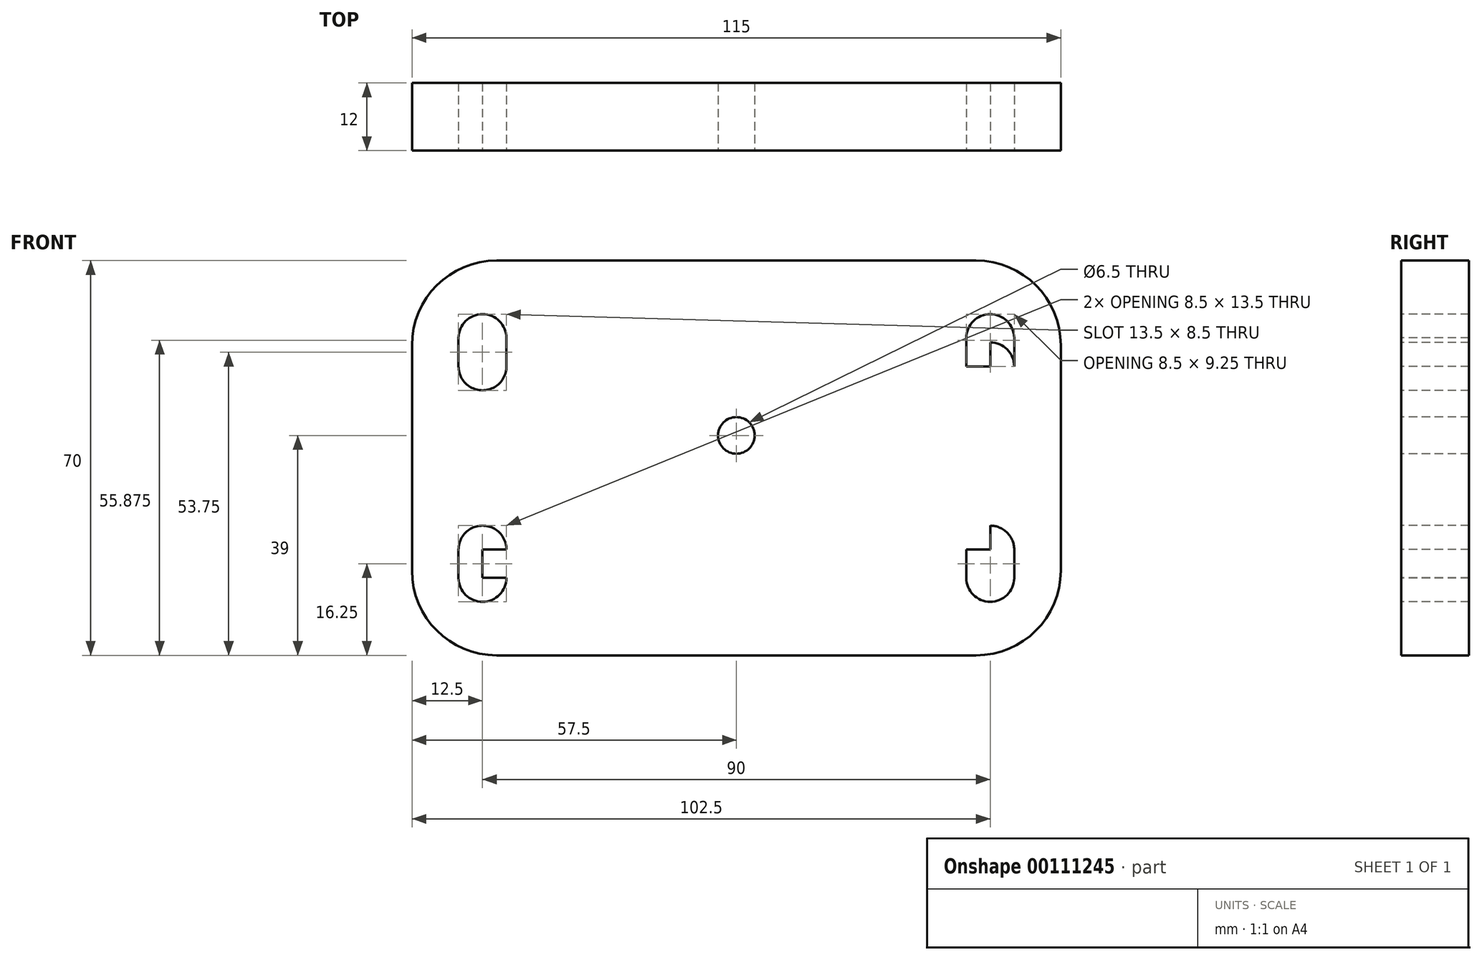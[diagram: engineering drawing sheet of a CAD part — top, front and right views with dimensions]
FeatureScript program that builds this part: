
annotation { "Feature Type Name" : "Feature", "Feature Type Description" : "" }
export const myFeature = defineFeature(function(context is Context, id is Id, definition is map)
    precondition{}
    {
        {
            var Q0;
            Q0=qCreatedBy(makeId("Front.planeOp"),FACE);
            var sketch = newSketch(context, id + "F0", { "sketchPlane" : qUnion([Q0])});
            skLineSegment(sketch, "E0.bottom", {"start": v(-57.5, 35) * mm, "end": v(57.5, 35) * mm});
            skLineSegment(sketch, "E0.top", {"start": v(-57.5, -35) * mm, "end": v(57.5, -35) * mm});
            skLineSegment(sketch, "E0.left", {"start": v(-57.5, 35) * mm, "end": v(-57.5, -35) * mm});
            skLineSegment(sketch, "E0.right", {"start": v(57.5, 35) * mm, "end": v(57.5, -35) * mm});
            skPoint(sketch, "E0.middle", {"position": v(0, 0) * mm});
            skSolve(sketch);
        }
        {
            var Q0;
            Q0 = qSketchRegion(id + "F0", true);
            extrude(context, id + "F1", {"entities" : qUnion([Q0]), "depth" : 12 * mm});
        }
        {
            var Q0;
            Q0=makeQuery(id+"F1.opExtrude","CAP_FACE",FACE,{"disambiguationData":[OSD([sQuery(id+"F0.wireOp",EDGE,"E0.bottom"),sQuery(id+"F0.wireOp",EDGE,"E0.top"),sQuery(id+"F0.wireOp",EDGE,"E0.left"),sQuery(id+"F0.wireOp",EDGE,"E0.right")])],"isStart":false});
            var sketch = newSketch(context, id + "F2", { "sketchPlane" : qUnion([Q0])});
            skLineSegment(sketch, "E1.bottom", {"start": v(-45, 21.25) * mm, "end": v(40.75, 21.25) * mm});
            skLineSegment(sketch, "E1.top", {"start": v(-45, -21.25) * mm, "end": v(45, -21.25) * mm});
            skLineSegment(sketch, "E1.left", {"start": v(-45, 16.25) * mm, "end": v(-45, -21.25) * mm});
            skLineSegment(sketch, "E1.right", {"start": v(45, 21.25) * mm, "end": v(45, -21.25) * mm});
            skPoint(sketch, "E1.middle", {"position": v(0, 0) * mm});
            skArc(sketch, "E2", {"start": v(-49.25, -21.2) * mm, "mid": v(-45.02, -25.5) * mm, "end": v(-40.75, -21.25) * mm});
            skArc(sketch, "E3.MirrorC", {"start": v(40.75, 21.25) * mm, "mid": v(45.02, 25.5) * mm, "end": v(49.25, 21.2) * mm});
            skLineSegment(sketch, "E4.bottom", {"start": v(-45, 16.25) * mm, "end": v(45, 16.25) * mm});
            skLineSegment(sketch, "E4.top", {"start": v(-45, -16.25) * mm, "end": v(45, -16.25) * mm});
            skLineSegment(sketch, "E4.left", {"start": v(-45, 16.25) * mm, "end": v(-45, -16.25) * mm});
            skLineSegment(sketch, "E4.right", {"start": v(45, 16.25) * mm, "end": v(45, -16.25) * mm});
            skArc(sketch, "E5", {"start": v(-49.25, 16.25) * mm, "mid": v(-45, 12) * mm, "end": v(-40.75, 16.25) * mm});
            skArc(sketch, "E6.MirrorC", {"start": v(49.25, 16.25) * mm, "mid": v(45, 12) * mm, "end": v(40.75, 16.25) * mm});
            skCircle(sketch, "E7.MirrorC", {"center": v(45, 16.25) * mm, "radius": 4.25 * mm});
            skArc(sketch, "E8.MirrorC", {"start": v(48.44, 18.75) * mm, "mid": v(46.31, 12.2) * mm, "end": v(40.75, 16.25) * mm});
            skArc(sketch, "E9.MirrorC", {"start": v(-49.25, -16.25) * mm, "mid": v(-45, -12) * mm, "end": v(-40.75, -16.25) * mm});
            skLineSegment(sketch, "E10", {"start": v(-49.25, 21.3) * mm, "end": v(-49.25, 16.25) * mm});
            skLineSegment(sketch, "E11", {"start": v(-40.75, 21.25) * mm, "end": v(-40.75, 16.25) * mm});
            skArc(sketch, "E12.trimOffspring", {"start": v(-40.75, 21.25) * mm, "mid": v(-45.02, 25.5) * mm, "end": v(-49.25, 21.2) * mm});
            skLineSegment(sketch, "E13.MirrorCS", {"start": v(40.75, 21.25) * mm, "end": v(40.75, 16.25) * mm});
            skLineSegment(sketch, "E14.MirrorCS", {"start": v(49.25, 21.3) * mm, "end": v(49.25, 16.25) * mm});
            skLineSegment(sketch, "E15.MirrorCS", {"start": v(-40.75, -21.25) * mm, "end": v(-40.75, -16.25) * mm});
            skLineSegment(sketch, "E16.MirrorCS", {"start": v(-49.25, -21.3) * mm, "end": v(-49.25, -16.25) * mm});
            skLineSegment(sketch, "E17.MirrorCS", {"start": v(40.75, -21.25) * mm, "end": v(40.75, -16.25) * mm});
            skLineSegment(sketch, "E18.MirrorCS", {"start": v(49.25, -21.3) * mm, "end": v(49.25, -16.25) * mm});
            skArc(sketch, "E19.trimOffspring", {"start": v(49.25, -16.25) * mm, "mid": v(45, -12) * mm, "end": v(40.75, -16.25) * mm});
            skArc(sketch, "E20.trimOffspring", {"start": v(49.25, -21.2) * mm, "mid": v(45.02, -25.5) * mm, "end": v(40.75, -21.25) * mm});
            skSolve(sketch);
        }
        {
            var Q0;
            {var subQ0=sQuery(id+"F2.wireOp",EDGE,"E4.left");var subQ1=sQuery(id+"F2.wireOp",EDGE,"E4.bottom");var subQ2=makeQuery(id+"F2.imprint","INTERSECT",VERTEX,{"derivedFrom":[subQ1,subQ0]});Q0=makeQuery(id+"F2.imprint","IMPRINT",FACE,{"disambiguationData":[TD([[makeQuery(id+"F2.imprint","IMPRINT",EDGE,{"disambiguationData":[TD([[subQ2,-1.0]])],"derivedFrom":subQ0}),1.0]])]});}
            var Q1;
            {var subQ10=sQuery(id+"F2.wireOp",EDGE,"E11");Q1=makeQuery(id+"F2.imprint","IMPRINT",FACE,{"disambiguationData":[TD([[makeQuery(id+"F2.imprint","IMPRINT",EDGE,{"derivedFrom":subQ10}),-1.0]])]});}
            var Q2;
            {var subQ0=sQuery(id+"F2.wireOp",EDGE,"E4.left");var subQ3=sQuery(id+"F2.wireOp",EDGE,"E9.MirrorC");var subQ5=makeQuery(id+"F2.imprint","INTERSECT",VERTEX,{"derivedFrom":[subQ0,subQ3]});Q2=makeQuery(id+"F2.imprint","IMPRINT",FACE,{"disambiguationData":[TD([[makeQuery(id+"F2.imprint","IMPRINT",EDGE,{"disambiguationData":[TD([[subQ5,-1.0]])],"derivedFrom":subQ0}),1.0]])]});}
            var Q3;
            {var subQ0=sQuery(id+"F2.wireOp",EDGE,"E1.left");Q3=makeQuery(id+"F2.imprint","IMPRINT",FACE,{"disambiguationData":[TD([[makeQuery(id+"F2.imprint","IMPRINT",EDGE,{"derivedFrom":subQ0}),1.0]])]});}
            var Q4;
            {var subQ1=sQuery(id+"F2.wireOp",EDGE,"E1.left");Q4=makeQuery(id+"F2.imprint","IMPRINT",FACE,{"disambiguationData":[TD([[makeQuery(id+"F2.imprint","IMPRINT",EDGE,{"derivedFrom":subQ1}),-1.0]])]});}
            var Q5;
            {var subQ0=sQuery(id+"F2.wireOp",EDGE,"E20.trimOffspring");var subQ1=sQuery(id+"F2.wireOp",EDGE,"E18.MirrorCS");var subQ2=makeQuery(id+"F2.imprint","INTERSECT",VERTEX,{"disambiguationData":[OD(0.0)],"derivedFrom":[subQ1,subQ0]});Q5=makeQuery(id+"F2.imprint","IMPRINT",FACE,{"disambiguationData":[TD([[makeQuery(id+"F2.imprint","IMPRINT",EDGE,{"disambiguationData":[TD([[subQ2,-1.0]])],"derivedFrom":subQ1}),1.0]])]});}
            var Q6;
            {var subQ3=sQuery(id+"F2.wireOp",EDGE,"E17.MirrorCS");Q6=makeQuery(id+"F2.imprint","IMPRINT",FACE,{"disambiguationData":[TD([[makeQuery(id+"F2.imprint","IMPRINT",EDGE,{"derivedFrom":subQ3}),-1.0]])]});}
            var Q7;
            {var subQ0=sQuery(id+"F2.wireOp",EDGE,"E4.right");var subQ3=sQuery(id+"F2.wireOp",EDGE,"E19.trimOffspring");var subQ5=makeQuery(id+"F2.imprint","INTERSECT",VERTEX,{"derivedFrom":[subQ0,subQ3]});Q7=makeQuery(id+"F2.imprint","IMPRINT",FACE,{"disambiguationData":[TD([[makeQuery(id+"F2.imprint","IMPRINT",EDGE,{"disambiguationData":[TD([[subQ5,-1.0]])],"derivedFrom":subQ0}),-1.0]])]});}
            var Q8;
            {var subQ0=sQuery(id+"F2.wireOp",EDGE,"E4.right");var subQ3=sQuery(id+"F2.wireOp",EDGE,"E7.MirrorC");var subQ5=makeQuery(id+"F2.imprint","INTERSECT",VERTEX,{"derivedFrom":[subQ0,subQ3]});Q8=makeQuery(id+"F2.imprint","IMPRINT",FACE,{"disambiguationData":[TD([[makeQuery(id+"F2.imprint","IMPRINT",EDGE,{"disambiguationData":[TD([[subQ5,1.0]])],"derivedFrom":subQ0}),-1.0]])]});}
            var Q9;
            {var subQ1=sQuery(id+"F2.wireOp",EDGE,"E1.right");var subQ3=sQuery(id+"F2.wireOp",EDGE,"E7.MirrorC");var subQ4=makeQuery(id+"F2.imprint","INTERSECT",VERTEX,{"derivedFrom":[subQ1,subQ3]});Q9=makeQuery(id+"F2.imprint","IMPRINT",FACE,{"disambiguationData":[TD([[makeQuery(id+"F2.imprint","IMPRINT",EDGE,{"disambiguationData":[TD([[subQ4,-1.0]])],"derivedFrom":subQ1}),-1.0]])]});}
            var Q10;
            {var subQ0=sQuery(id+"F2.wireOp",EDGE,"E7.MirrorC");var subQ2=makeQuery(id+"F2.imprint","IMPRINT",VERTEX,{"derivedFrom":subQ0});Q10=makeQuery(id+"F2.imprint","IMPRINT",FACE,{"disambiguationData":[TD([[makeQuery(id+"F2.imprint","IMPRINT",EDGE,{"disambiguationData":[TD([[subQ2,1.0]])],"derivedFrom":subQ0}),-1.0]])]});}
            var Q11;
            {var subQ4=sQuery(id+"F2.wireOp",EDGE,"E13.MirrorCS");Q11=makeQuery(id+"F2.imprint","IMPRINT",FACE,{"disambiguationData":[TD([[makeQuery(id+"F2.imprint","IMPRINT",EDGE,{"derivedFrom":subQ4}),1.0]])]});}
            extrude(context, id + "F3", {"entities" : qUnion([Q0, Q1, Q2, Q3, Q4, Q5, Q6, Q7, Q8, Q9, Q10, Q11]), "operationType" : NewBodyOperationType.REMOVE, "oppositeDirection" : true, "depth" : 25 * mm});
        }
        {
            var Q0;
            Q0=makeQuery(id+"F1.opExtrude","CAP_FACE",FACE,{"disambiguationData":[OSD([sQuery(id+"F0.wireOp",EDGE,"E0.bottom"),sQuery(id+"F0.wireOp",EDGE,"E0.top"),sQuery(id+"F0.wireOp",EDGE,"E0.left"),sQuery(id+"F0.wireOp",EDGE,"E0.right")])],"isStart":false});
            var sketch = newSketch(context, id + "F4", { "sketchPlane" : qUnion([Q0])});
            skPoint(sketch, "E21", {"position": v(0, 4) * mm});
            skCircle(sketch, "E22", {"center": v(0, 4) * mm, "radius": 3.25 * mm});
            skSolve(sketch);
        }
        {
            var Q0;
            Q0 = qSketchRegion(id + "F4", true);
            extrude(context, id + "F5", {"entities" : qUnion([Q0]), "operationType" : NewBodyOperationType.REMOVE, "oppositeDirection" : true, "depth" : 25 * mm});
        }
        {
            var Q0;
            Q0=makeQuery(id+"F1.opExtrude","SWEPT_EDGE",EDGE,{"disambiguationData":[OSD([sQuery(id+"F0.wireOp",EDGE,"E0.bottom"),sQuery(id+"F0.wireOp",EDGE,"E0.left")])]});
            var Q1;
            Q1=makeQuery(id+"F1.opExtrude","SWEPT_EDGE",EDGE,{"disambiguationData":[OSD([sQuery(id+"F0.wireOp",EDGE,"E0.bottom"),sQuery(id+"F0.wireOp",EDGE,"E0.right")])]});
            var Q2;
            Q2=makeQuery(id+"F1.opExtrude","SWEPT_EDGE",EDGE,{"disambiguationData":[OSD([sQuery(id+"F0.wireOp",EDGE,"E0.top"),sQuery(id+"F0.wireOp",EDGE,"E0.right")])]});
            var Q3;
            Q3=makeQuery(id+"F1.opExtrude","SWEPT_EDGE",EDGE,{"disambiguationData":[OSD([sQuery(id+"F0.wireOp",EDGE,"E0.top"),sQuery(id+"F0.wireOp",EDGE,"E0.left")])]});
            fillet(context, id + "F6", {"entities" : qUnion([Q0, Q1, Q2, Q3]), "radius" : 15 * mm, "tangentPropagation" : true, "allowEdgeOverflow" : false});
        }
    });
